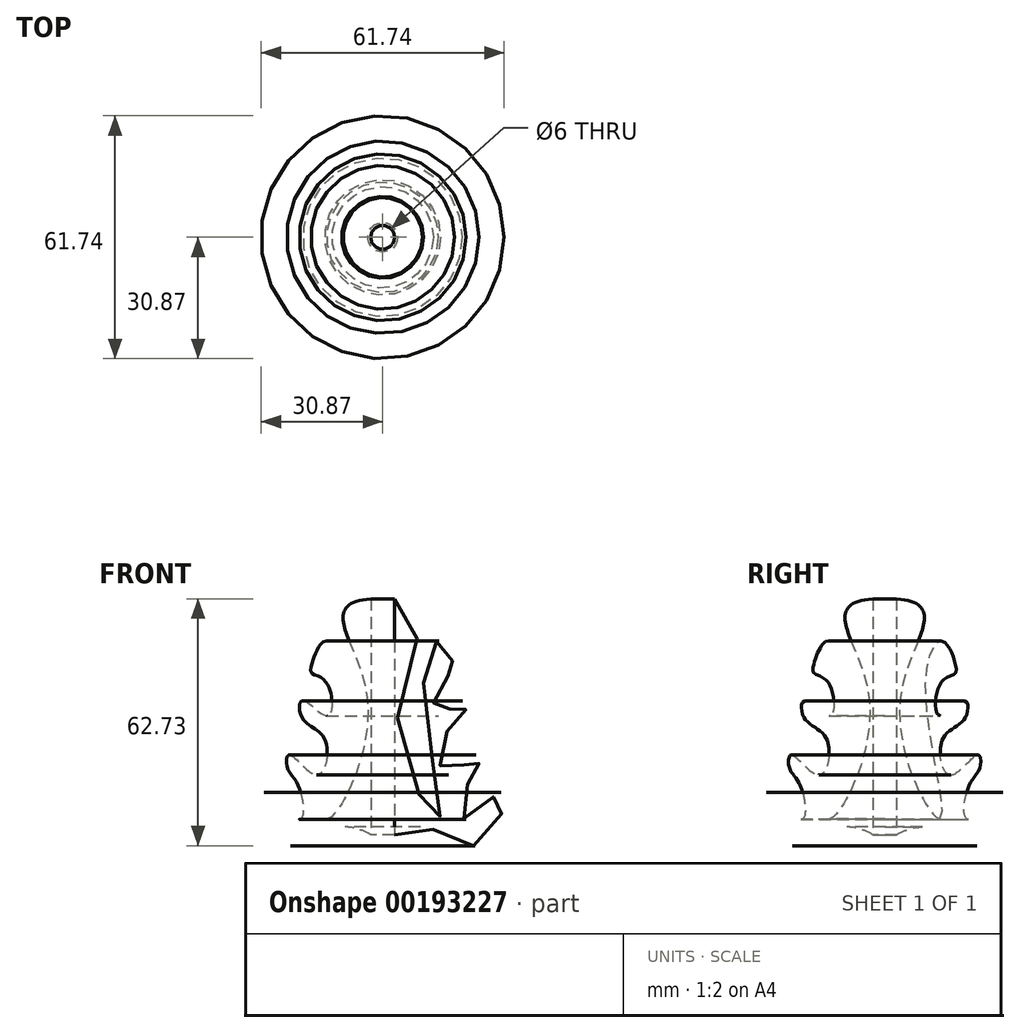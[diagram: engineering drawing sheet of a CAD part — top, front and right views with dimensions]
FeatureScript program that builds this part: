
annotation { "Feature Type Name" : "Feature", "Feature Type Description" : "" }
export const myFeature = defineFeature(function(context is Context, id is Id, definition is map)
    precondition{}
    {
        {
            var Q0;
            Q0=qCreatedBy(makeId("Right.planeOp"),FACE);
            var sketch = newSketch(context, id + "F0", { "sketchPlane" : qUnion([Q0])});
            skFitSpline(sketch, "E0", {"points": [v(0, 0) * mm, v(-11.72, 3.81) * mm, v(-25.81, 0) * mm, v(-30.24, 12.84) * mm, v(-21.17, 6.02) * mm, v(-21.52, 14.78) * mm, v(-24.17, 18.95) * mm, v(-23.7, 22.33) * mm, v(-16.68, 17.3) * mm, v(-14.67, 26.23) * mm, v(-20.4, 31.72) * mm, v(-20.32, 36.13) * mm, v(-13.98, 32.33) * mm, v(-14.14, 40.49) * mm, v(-17.8, 43) * mm, v(-18.2, 44.43) * mm, v(-14.84, 51.26) * mm, v(-10.4, 40.32) * mm, v(-14.2, 6.15) * mm, v(-4.23, 38.88) * mm, v(0, 62.1) * mm], "startDerivative": vector(-159.68, 129.16) * mm, "endDerivative": vector(720.52, -6.88) * mm});
            skLineSegment(sketch, "E1", {"start": v(0, 62.1) * mm, "end": v(0, 0) * mm});
            skSolve(sketch);
        }
        {
            var Q0;
            Q0=makeQuery(id+"F0.imprint","IMPRINT",FACE,{"disambiguationData":[TD([[makeQuery(id+"F0.imprint","IMPRINT",EDGE,{"derivedFrom":sQuery(id+"F0.wireOp",EDGE,"E0")}),-1.0]])]});
            var Q1;
            Q1=sQuery(id+"F0.wireOp",EDGE,"E1");
            revolve(context, id + "F1", {"entities" : qUnion([Q0]), "axis" : qUnion([Q1]), "revolveType" : RevolveType.FULL});
        }
        {
            var Q0;
            Q0=qCreatedBy(makeId("Top.planeOp"),FACE);
            var sketch = newSketch(context, id + "F2", { "sketchPlane" : qUnion([Q0])});
            skCircle(sketch, "E2", {"center": v(0, 0) * mm, "radius": 3 * mm});
            skSolve(sketch);
        }
        {
            var Q0;
            Q0=qSketchRegion(id+"F2",true);
            var Q1;
            Q1=makeQuery(id+"F1.opRevolve","SWEPT_FACE",FACE,{"disambiguationData":[OSD([sQuery(id+"F0.wireOp",EDGE,"E0")])]});
            extrude(context, id + "F3", {"entities" : qUnion([Q0]), "operationType" : NewBodyOperationType.REMOVE, "endBoundEntityFace" : qUnion([Q1]), "depth" : 65.53 * mm});
        }
    });
